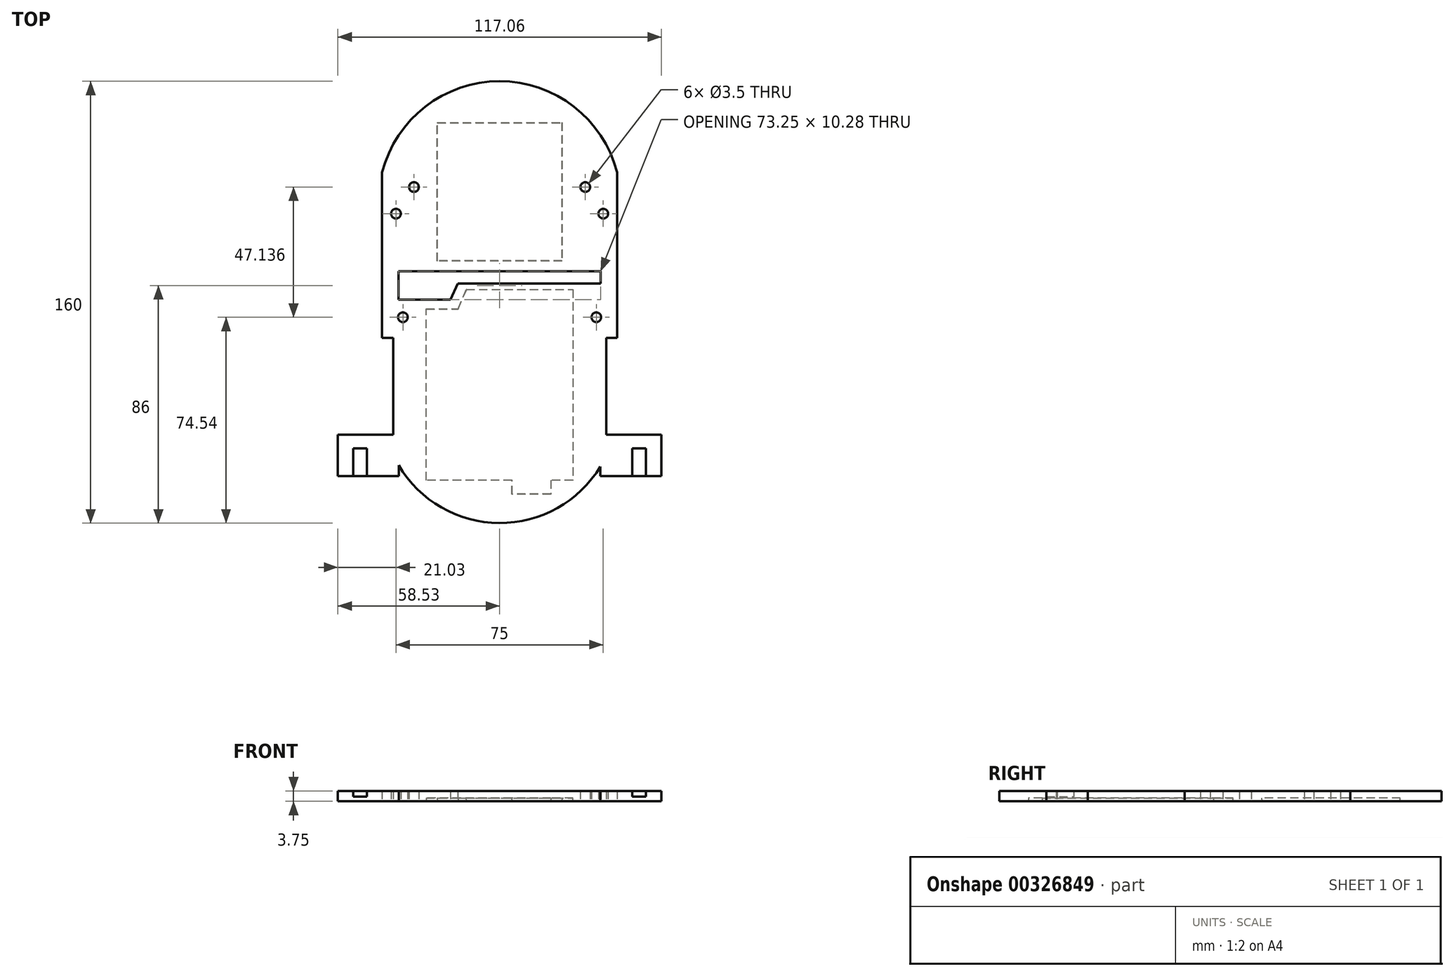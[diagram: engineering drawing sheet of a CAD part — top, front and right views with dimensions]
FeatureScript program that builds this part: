
annotation { "Feature Type Name" : "Feature", "Feature Type Description" : "" }
export const myFeature = defineFeature(function(context is Context, id is Id, definition is map)
    precondition{}
    {
        {
            var Q0;
            Q0=qCreatedBy(makeId("Top.planeOp"),FACE);
            var sketch = newSketch(context, id + "F0", { "sketchPlane" : qUnion([Q0])});
            skLineSegment(sketch, "E0.left", {"start": v(42.5, 30) * mm, "end": v(42.5, -30) * mm});
            skLineSegment(sketch, "E0.right", {"start": v(-42.5, 30) * mm, "end": v(-42.5, -30) * mm});
            skPoint(sketch, "E0.middle", {"position": v(0, 0) * mm});
            skArc(sketch, "E1", {"start": v(42.5, 30) * mm, "mid": v(0, 62.96) * mm, "end": v(-42.5, 30) * mm});
            skLineSegment(sketch, "E2.bottom", {"start": v(66.5, -30) * mm, "end": v(42.5, -30) * mm});
            skLineSegment(sketch, "E2.top", {"start": v(66.5, -80) * mm, "end": v(36.5, -80) * mm});
            skLineSegment(sketch, "E2.left", {"start": v(66.5, -30) * mm, "end": v(66.5, -80) * mm});
            skLineSegment(sketch, "E3.bottom", {"start": v(-66.5, -30) * mm, "end": v(-42.5, -30) * mm});
            skLineSegment(sketch, "E3.top", {"start": v(-66.5, -80) * mm, "end": v(-36.5, -80) * mm});
            skLineSegment(sketch, "E3.left", {"start": v(-66.5, -30) * mm, "end": v(-66.5, -80) * mm});
            skPoint(sketch, "E4.endSnap0", {"position": v(0, -30) * mm});
            skPoint(sketch, "E5.second.point", {"position": v(0, -12.04) * mm});
            skPoint(sketch, "E5.third.point", {"position": v(-39.19, -70.68) * mm});
            skArc(sketch, "E6.trimOffspring", {"start": v(-36.5, -76.09) * mm, "mid": v(-0.12, -97.04) * mm, "end": v(36.5, -76.52) * mm});
            skLineSegment(sketch, "E7.trimOffspring", {"start": v(-36.5, -76.09) * mm, "end": v(-36.5, -80) * mm});
            skLineSegment(sketch, "E8.trimOffspring", {"start": v(36.5, -76.52) * mm, "end": v(36.5, -80) * mm});
            skSolve(sketch);
        }
        {
            var Q0;
            Q0=makeQuery(id+"F0.imprint","IMPRINT",FACE,{"disambiguationData":[TD([[makeQuery(id+"F0.imprint","IMPRINT",EDGE,{"derivedFrom":sQuery(id+"F0.wireOp",EDGE,"E0.left")}),-1.0]])]});
            extrude(context, id + "F1", {"entities" : qUnion([Q0]), "depth" : 5 * mm});
        }
        {
            var Q0;
            Q0=qCreatedBy(makeId("Top.planeOp"),FACE);
            var sketch = newSketch(context, id + "F2", { "sketchPlane" : qUnion([Q0])});
            skLineSegment(sketch, "E9.bottom", {"start": v(22.5, 47.94) * mm, "end": v(-22.5, 47.94) * mm});
            skLineSegment(sketch, "E9.top", {"start": v(22.5, -2.06) * mm, "end": v(-22.5, -2.06) * mm});
            skLineSegment(sketch, "E9.left", {"start": v(22.5, 47.94) * mm, "end": v(22.5, -2.06) * mm});
            skLineSegment(sketch, "E9.right", {"start": v(-22.5, 47.94) * mm, "end": v(-22.5, -2.06) * mm});
            skPoint(sketch, "E9.middle", {"position": v(0, 22.94) * mm});
            skLineSegment(sketch, "E10.bottom", {"start": v(26.5, -12.51) * mm, "end": v(-12, -12.51) * mm});
            skLineSegment(sketch, "E10.left", {"start": v(26.5, -12.51) * mm, "end": v(26.5, -81.51) * mm});
            skLineSegment(sketch, "E10.right", {"start": v(-26.5, -19.51) * mm, "end": v(-26.5, -81.51) * mm});
            skPoint(sketch, "E10.middle", {"position": v(0, -47.01) * mm});
            skLineSegment(sketch, "E11.top", {"start": v(-26.5, -19.51) * mm, "end": v(-15, -19.51) * mm});
            skLineSegment(sketch, "E12", {"start": v(-15, -19.51) * mm, "end": v(-12, -12.51) * mm});
            skLineSegment(sketch, "E13", {"start": v(26.5, -81.51) * mm, "end": v(18.5, -81.51) * mm});
            skLineSegment(sketch, "E14.top", {"start": v(18.5, -86.51) * mm, "end": v(4.5, -86.51) * mm});
            skLineSegment(sketch, "E14.left", {"start": v(18.5, -81.51) * mm, "end": v(18.5, -86.51) * mm});
            skLineSegment(sketch, "E14.right", {"start": v(4.5, -81.51) * mm, "end": v(4.5, -86.51) * mm});
            skLineSegment(sketch, "E15", {"start": v(-26.5, -81.51) * mm, "end": v(4.5, -81.51) * mm});
            skSolve(sketch);
        }
        {
            var Q0;
            Q0=makeQuery(id+"F1.opExtrude","CAP_FACE",FACE,{"disambiguationData":[OSD([sQuery(id+"F0.wireOp",EDGE,"E0.left"),sQuery(id+"F0.wireOp",EDGE,"E0.right"),sQuery(id+"F0.wireOp",EDGE,"E1"),sQuery(id+"F0.wireOp",EDGE,"E2.top"),sQuery(id+"F0.wireOp",EDGE,"E2.left"),sQuery(id+"F0.wireOp",EDGE,"E2.bottom"),sQuery(id+"F0.wireOp",EDGE,"E3.top"),sQuery(id+"F0.wireOp",EDGE,"E3.left"),sQuery(id+"F0.wireOp",EDGE,"E3.bottom"),sQuery(id+"F0.wireOp",EDGE,"E6.trimOffspring"),sQuery(id+"F0.wireOp",EDGE,"E7.trimOffspring"),sQuery(id+"F0.wireOp",EDGE,"E8.trimOffspring")])],"isStart":false});
            var Q1;
            Q1=qSketchRegion(id+"F2",true);
            extrude(context, id + "F3", {"entities" : qUnion([Q0, Q1]), "operationType" : NewBodyOperationType.REMOVE, "endBound" : BoundingType.SYMMETRIC, "depth" : 2.5 * mm, "hasDraft" : true, "draftAngle" : 3 * degree});
        }
        {
            var Q0;
            Q0=qCreatedBy(makeId("Top.planeOp"),FACE);
            var sketch = newSketch(context, id + "F4", { "sketchPlane" : qUnion([Q0])});
            skLineSegment(sketch, "E16.bottom", {"start": v(58.53, -65) * mm, "end": v(38.53, -64.97) * mm});
            skLineSegment(sketch, "E16.right", {"start": v(38.53, -64.97) * mm, "end": v(38.53, -30) * mm});
            skLineSegment(sketch, "E17.top", {"start": v(58.53, -80) * mm, "end": v(66.5, -80) * mm});
            skLineSegment(sketch, "E17.left", {"start": v(58.53, -65) * mm, "end": v(58.53, -80) * mm});
            skLineSegment(sketch, "E18.top", {"start": v(38.53, -65) * mm, "end": v(58.53, -65) * mm});
            skLineSegment(sketch, "E18.left", {"start": v(38.53, -30) * mm, "end": v(38.53, -65) * mm});
            skLineSegment(sketch, "E19", {"start": v(38.53, -30) * mm, "end": v(66.5, -30) * mm});
            skLineSegment(sketch, "E20", {"start": v(66.5, -80) * mm, "end": v(66.5, -30) * mm});
            skLineSegment(sketch, "E21.bottom", {"start": v(-66.5, -30) * mm, "end": v(-38.53, -30) * mm});
            skLineSegment(sketch, "E21.top", {"start": v(-58.53, -65) * mm, "end": v(-38.53, -65) * mm});
            skLineSegment(sketch, "E21.right", {"start": v(-38.53, -30) * mm, "end": v(-38.53, -65) * mm});
            skLineSegment(sketch, "E22.top", {"start": v(-66.5, -80) * mm, "end": v(-58.53, -80) * mm});
            skLineSegment(sketch, "E22.right", {"start": v(-58.53, -65) * mm, "end": v(-58.53, -80) * mm});
            skLineSegment(sketch, "E23", {"start": v(-66.5, -30) * mm, "end": v(-66.5, -80) * mm});
            skSolve(sketch);
        }
        {
            var Q0;
            Q0=qSketchRegion(id+"F4",true);
            extrude(context, id + "F5", {"entities" : qUnion([Q0]), "operationType" : NewBodyOperationType.REMOVE, "depth" : 25 * mm});
        }
        {
            var Q0;
            Q0=qCreatedBy(makeId("Top.planeOp"),FACE);
            var sketch = newSketch(context, id + "F6", { "sketchPlane" : qUnion([Q0])});
            skPoint(sketch, "E24.middle", {"position": v(35, -22.5) * mm});
            skCircle(sketch, "E25", {"center": v(35, -22.5) * mm, "radius": 1.75 * mm});
            skPoint(sketch, "E26.middle", {"position": v(-35, -22.5) * mm});
            skCircle(sketch, "E27", {"center": v(-35, -22.5) * mm, "radius": 1.75 * mm});
            skPoint(sketch, "E28.middle", {"position": v(37.5, 15) * mm});
            skCircle(sketch, "E29", {"center": v(37.5, 15) * mm, "radius": 1.75 * mm});
            skPoint(sketch, "E30.middle", {"position": v(-37.5, 15) * mm});
            skCircle(sketch, "E31", {"center": v(-37.5, 15) * mm, "radius": 1.75 * mm});
            skPoint(sketch, "E32.middle", {"position": v(31, 24.64) * mm});
            skPoint(sketch, "E33.middle", {"position": v(-31, 24.64) * mm});
            skCircle(sketch, "E34", {"center": v(-31, 24.64) * mm, "radius": 1.75 * mm});
            skCircle(sketch, "E35", {"center": v(31, 24.64) * mm, "radius": 1.75 * mm});
            skLineSegment(sketch, "E36.bottom", {"start": v(-36.63, -5.9) * mm, "end": v(36.63, -5.9) * mm});
            skLineSegment(sketch, "E36.top", {"start": v(-15.1, -10.23) * mm, "end": v(36.63, -10.23) * mm});
            skLineSegment(sketch, "E36.left", {"start": v(-36.63, -5.9) * mm, "end": v(-36.63, -10.23) * mm});
            skLineSegment(sketch, "E36.right", {"start": v(36.63, -5.9) * mm, "end": v(36.63, -10.23) * mm});
            skLineSegment(sketch, "E37", {"start": v(-17.75, -16.18) * mm, "end": v(-15.1, -10.23) * mm});
            skLineSegment(sketch, "E38.top", {"start": v(-36.63, -16.18) * mm, "end": v(-17.75, -16.18) * mm});
            skLineSegment(sketch, "E38.left", {"start": v(-36.63, -10.23) * mm, "end": v(-36.63, -16.18) * mm});
            skSolve(sketch);
        }
        {
            var Q0;
            Q0 = qSketchRegion(id + "F6", true);
            extrude(context, id + "F7", {"entities" : qUnion([Q0]), "operationType" : NewBodyOperationType.REMOVE, "depth" : 25 * mm});
        }
        {
            var Q0;
            Q0=makeQuery(id+"F3.boolean.opBoolean","COPY",FACE,{"derivedFrom":makeQuery(id+"F3.opExtrude","CAP_FACE",FACE,{"disambiguationData":[OSD([sQuery(id+"F0.wireOp",EDGE,"E0.left"),sQuery(id+"F0.wireOp",EDGE,"E0.right"),sQuery(id+"F0.wireOp",EDGE,"E1"),sQuery(id+"F0.wireOp",EDGE,"E2.top"),sQuery(id+"F0.wireOp",EDGE,"E2.left"),sQuery(id+"F0.wireOp",EDGE,"E2.bottom"),sQuery(id+"F0.wireOp",EDGE,"E3.top"),sQuery(id+"F0.wireOp",EDGE,"E3.left"),sQuery(id+"F0.wireOp",EDGE,"E3.bottom"),sQuery(id+"F0.wireOp",EDGE,"E6.trimOffspring"),sQuery(id+"F0.wireOp",EDGE,"E7.trimOffspring"),sQuery(id+"F0.wireOp",EDGE,"E8.trimOffspring")])],"isStart":true})});
            var sketch = newSketch(context, id + "F8", { "sketchPlane" : qUnion([Q0])});
            skLineSegment(sketch, "E39.bottom", {"start": v(53, -80) * mm, "end": v(48, -80) * mm});
            skLineSegment(sketch, "E39.top", {"start": v(53, -70) * mm, "end": v(48, -70) * mm});
            skLineSegment(sketch, "E39.left", {"start": v(53, -80) * mm, "end": v(53, -70) * mm});
            skLineSegment(sketch, "E39.right", {"start": v(48, -80) * mm, "end": v(48, -70) * mm});
            skLineSegment(sketch, "E40.bottom", {"start": v(-53, -80) * mm, "end": v(-48, -80) * mm});
            skLineSegment(sketch, "E40.top", {"start": v(-53, -70) * mm, "end": v(-48, -70) * mm});
            skLineSegment(sketch, "E40.left", {"start": v(-53, -80) * mm, "end": v(-53, -70) * mm});
            skLineSegment(sketch, "E40.right", {"start": v(-48, -80) * mm, "end": v(-48, -70) * mm});
            skSolve(sketch);
        }
        {
            var Q0;
            Q0 = qSketchRegion(id + "F8", true);
            extrude(context, id + "F9", {"entities" : qUnion([Q0]), "operationType" : NewBodyOperationType.REMOVE, "oppositeDirection" : true, "depth" : 2 * mm});
        }
    });
